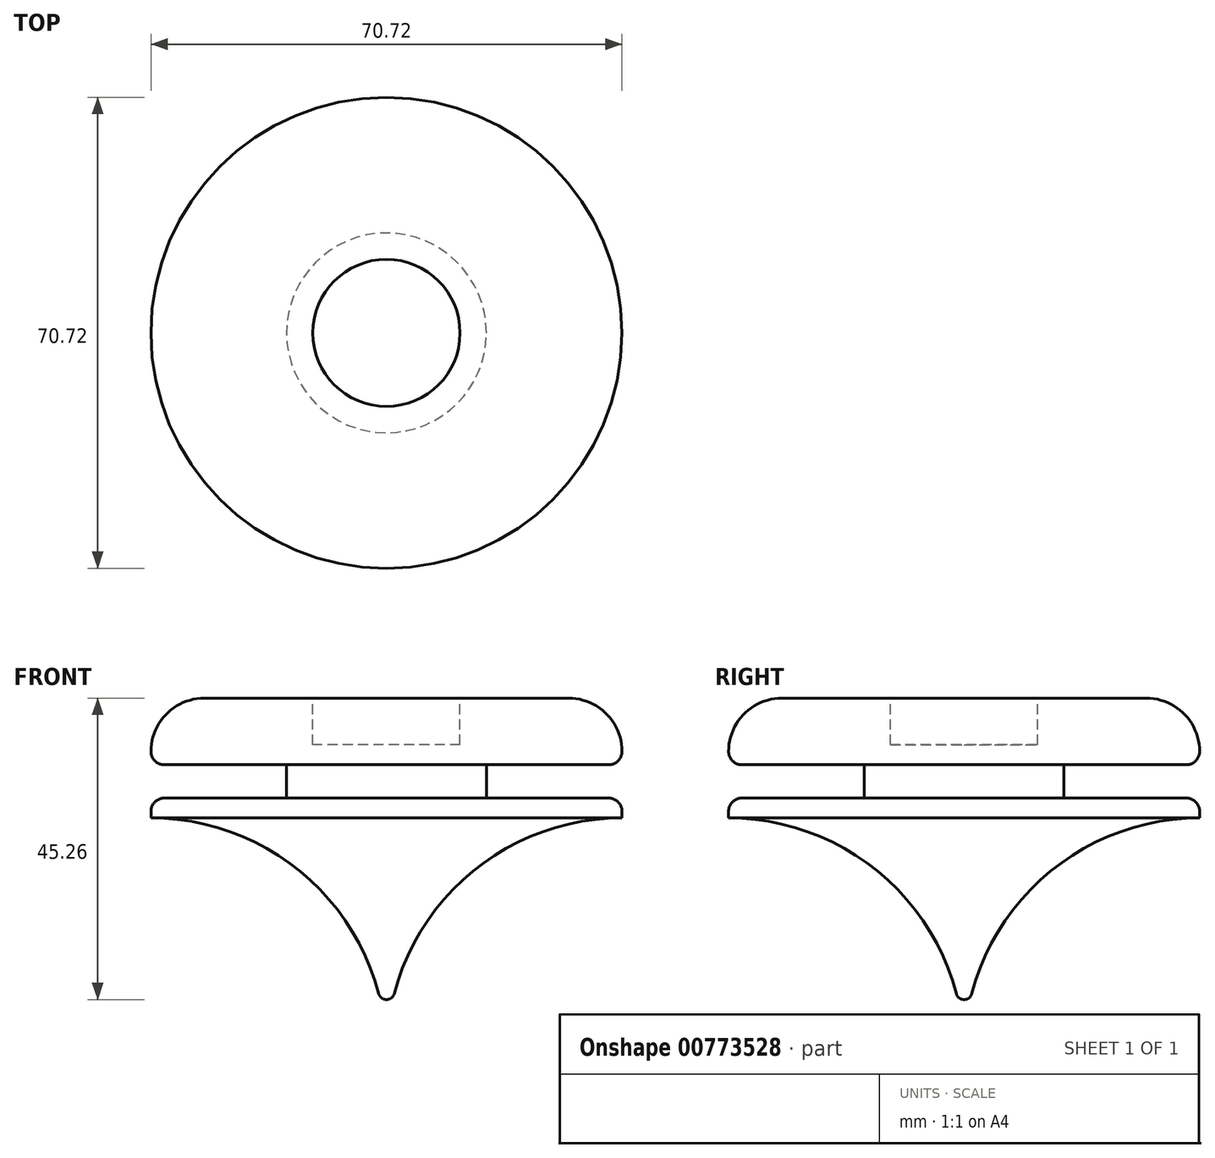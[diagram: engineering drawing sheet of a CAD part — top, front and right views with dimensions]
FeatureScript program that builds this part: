
annotation { "Feature Type Name" : "Feature", "Feature Type Description" : "" }
export const myFeature = defineFeature(function(context is Context, id is Id, definition is map)
    precondition{}
    {
        {
            var Q0;
            Q0=qCreatedBy(makeId("Top.planeOp"),FACE);
            cPlane(context, id + "F0", {"entities" : qUnion([Q0]), "cplaneType" : CPlaneType.OFFSET, "offset" : 18 * mm, "width" : 150 * mm, "height" : 150 * mm});
        }
        {
            var Q0;
            Q0=qCreatedBy(makeId("Front.planeOp"),FACE);
            var sketch = newSketch(context, id + "F1", { "sketchPlane" : qUnion([Q0])});
            skCircle(sketch, "E0", {"center": v(0, 0) * mm, "radius": 50 * mm, "construction": true});
            skArc(sketch, "E1", {"start": v(-1.16, -26.37) * mm, "mid": v(-13.77, -7.36) * mm, "end": v(-35.36, 0) * mm});
            skLineSegment(sketch, "E2.top", {"start": v(0, -35.36) * mm, "end": v(-35.36, -35.36) * mm, "construction": true});
            skLineSegment(sketch, "E2.left", {"start": v(0, 0) * mm, "end": v(0, -27.26) * mm});
            skLineSegment(sketch, "E2.right", {"start": v(-35.36, 0) * mm, "end": v(-35.36, -35.36) * mm, "construction": true});
            skLineSegment(sketch, "E3.top", {"start": v(-33.36, 3) * mm, "end": v(0, 3) * mm});
            skLineSegment(sketch, "E3.left", {"start": v(-35.36, 0) * mm, "end": v(-35.36, 1) * mm});
            skLineSegment(sketch, "E3.right", {"start": v(0, 0) * mm, "end": v(0, 3) * mm});
            skPoint(sketch, "E4.visualSharp", {"position": v(-35.36, 3) * mm});
            skArc(sketch, "E4.filletArc", {"start": v(-33.36, 3) * mm, "mid": v(-34.77, 2.41) * mm, "end": v(-35.36, 1) * mm});
            skLineSegment(sketch, "E5.bottom", {"start": v(0, 3) * mm, "end": v(-15, 3) * mm});
            skLineSegment(sketch, "E5.top", {"start": v(0, 8) * mm, "end": v(-15, 8) * mm});
            skLineSegment(sketch, "E5.left", {"start": v(0, 3) * mm, "end": v(0, 8) * mm});
            skLineSegment(sketch, "E5.right", {"start": v(-15, 3) * mm, "end": v(-15, 8) * mm});
            skLineSegment(sketch, "E6", {"start": v(-35.36, 0) * mm, "end": v(-35.36, 35.36) * mm, "construction": true});
            skLineSegment(sketch, "E7.bottom", {"start": v(0, 8) * mm, "end": v(-33.36, 8) * mm});
            skLineSegment(sketch, "E7.top", {"start": v(0, 18) * mm, "end": v(-27.36, 18) * mm});
            skLineSegment(sketch, "E7.left", {"start": v(0, 8) * mm, "end": v(0, 18) * mm});
            skLineSegment(sketch, "E7.right", {"start": v(-35.36, 10) * mm, "end": v(-35.36, 10) * mm});
            skPoint(sketch, "E8.visualSharp", {"position": v(-35.36, 18) * mm});
            skArc(sketch, "E8.filletArc", {"start": v(-27.36, 18) * mm, "mid": v(-33.01, 15.66) * mm, "end": v(-35.36, 10) * mm});
            skPoint(sketch, "E9.visualSharp", {"position": v(-35.36, 8) * mm});
            skArc(sketch, "E9.filletArc", {"start": v(-35.36, 10) * mm, "mid": v(-34.77, 8.59) * mm, "end": v(-33.36, 8) * mm});
            skArc(sketch, "E10", {"start": v(-1.16, -26.37) * mm, "mid": v(-0.73, -27.01) * mm, "end": v(0, -27.26) * mm});
            skSolve(sketch);
        }
        {
            var Q0;
            Q0 = qSketchRegion(id + "F1", true);
            var Q1;
            Q1=sQuery(id+"F1.wireOp",EDGE,"E3.right");
            revolve(context, id + "F2", {"surfaceOperationType" : NewSurfaceOperationType.NEW, "entities" : qUnion([Q0]), "axis" : qUnion([Q1]), "revolveType" : RevolveType.FULL});
        }
        {
            var Q0;
            Q0=qCreatedBy(id+"F0.planeOp",FACE);
            var sketch = newSketch(context, id + "F3", { "sketchPlane" : qUnion([Q0])});
            skCircle(sketch, "E11", {"center": v(0, 0) * mm, "radius": 11.05 * mm});
            skSolve(sketch);
        }
        {
            var Q0;
            Q0 = qSketchRegion(id + "F3", true);
            extrude(context, id + "F4", {"entities" : qUnion([Q0]), "operationType" : NewBodyOperationType.REMOVE, "oppositeDirection" : true, "depth" : 7 * mm, "offsetDistance" : 25 * mm});
        }
    });
